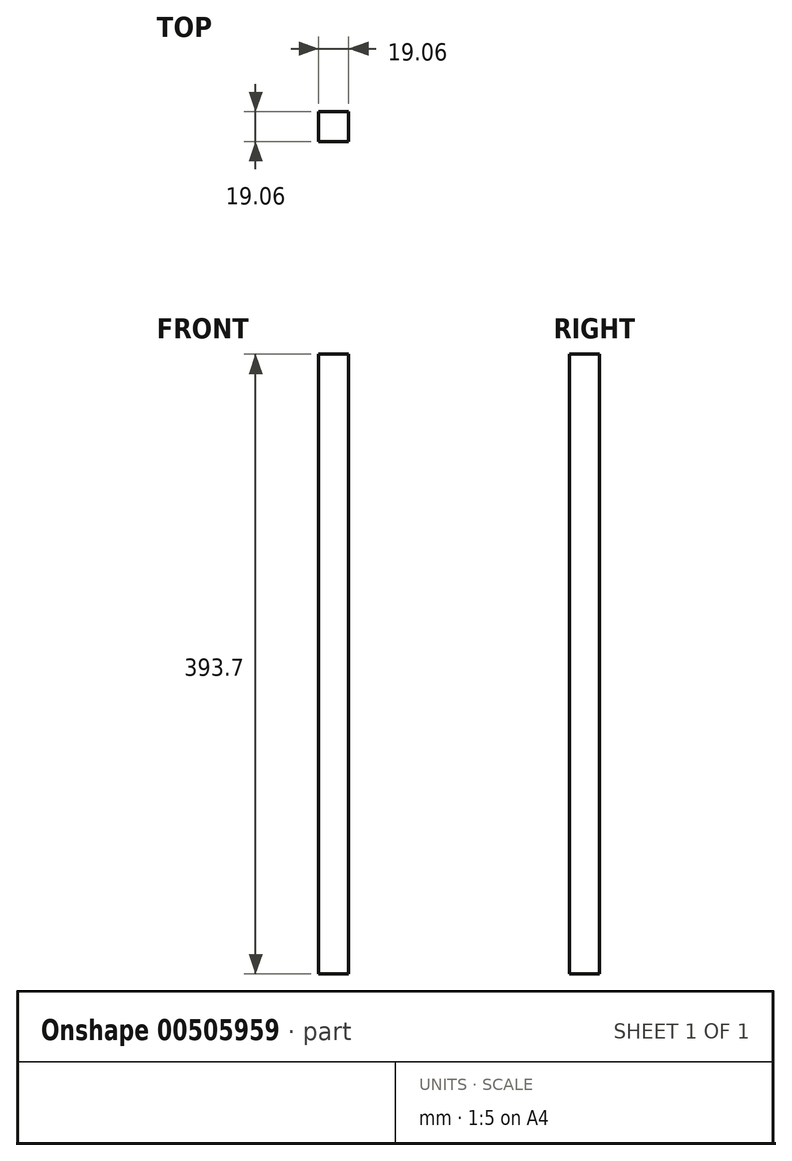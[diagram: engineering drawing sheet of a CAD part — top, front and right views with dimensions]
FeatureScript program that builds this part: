
annotation { "Feature Type Name" : "Feature", "Feature Type Description" : "" }
export const myFeature = defineFeature(function(context is Context, id is Id, definition is map)
    precondition{}
    {
        {
            var Q0;
            Q0=qCreatedBy(makeId("Top.planeOp"),FACE);
            var sketch = newSketch(context, id + "F0", { "sketchPlane" : qUnion([Q0])});
            skLineSegment(sketch, "E0.bottom", {"start": v(-9.53, 9.53) * mm, "end": v(9.53, 9.53) * mm});
            skLineSegment(sketch, "E0.top", {"start": v(-9.53, -9.53) * mm, "end": v(9.52, -9.53) * mm});
            skLineSegment(sketch, "E0.left", {"start": v(-9.53, 9.53) * mm, "end": v(-9.53, -9.53) * mm});
            skLineSegment(sketch, "E0.right", {"start": v(9.53, 9.53) * mm, "end": v(9.52, -9.53) * mm});
            skPoint(sketch, "E0.middle", {"position": v(0, 0) * mm});
            skSolve(sketch);
        }
        {
            var Q0;
            Q0=qSketchRegion(id+"F0",true);
            extrude(context, id + "F1", {"entities" : qUnion([Q0]), "depth" : 393.7 * mm, "offsetDistance" : 25.4 * mm});
        }
    });
